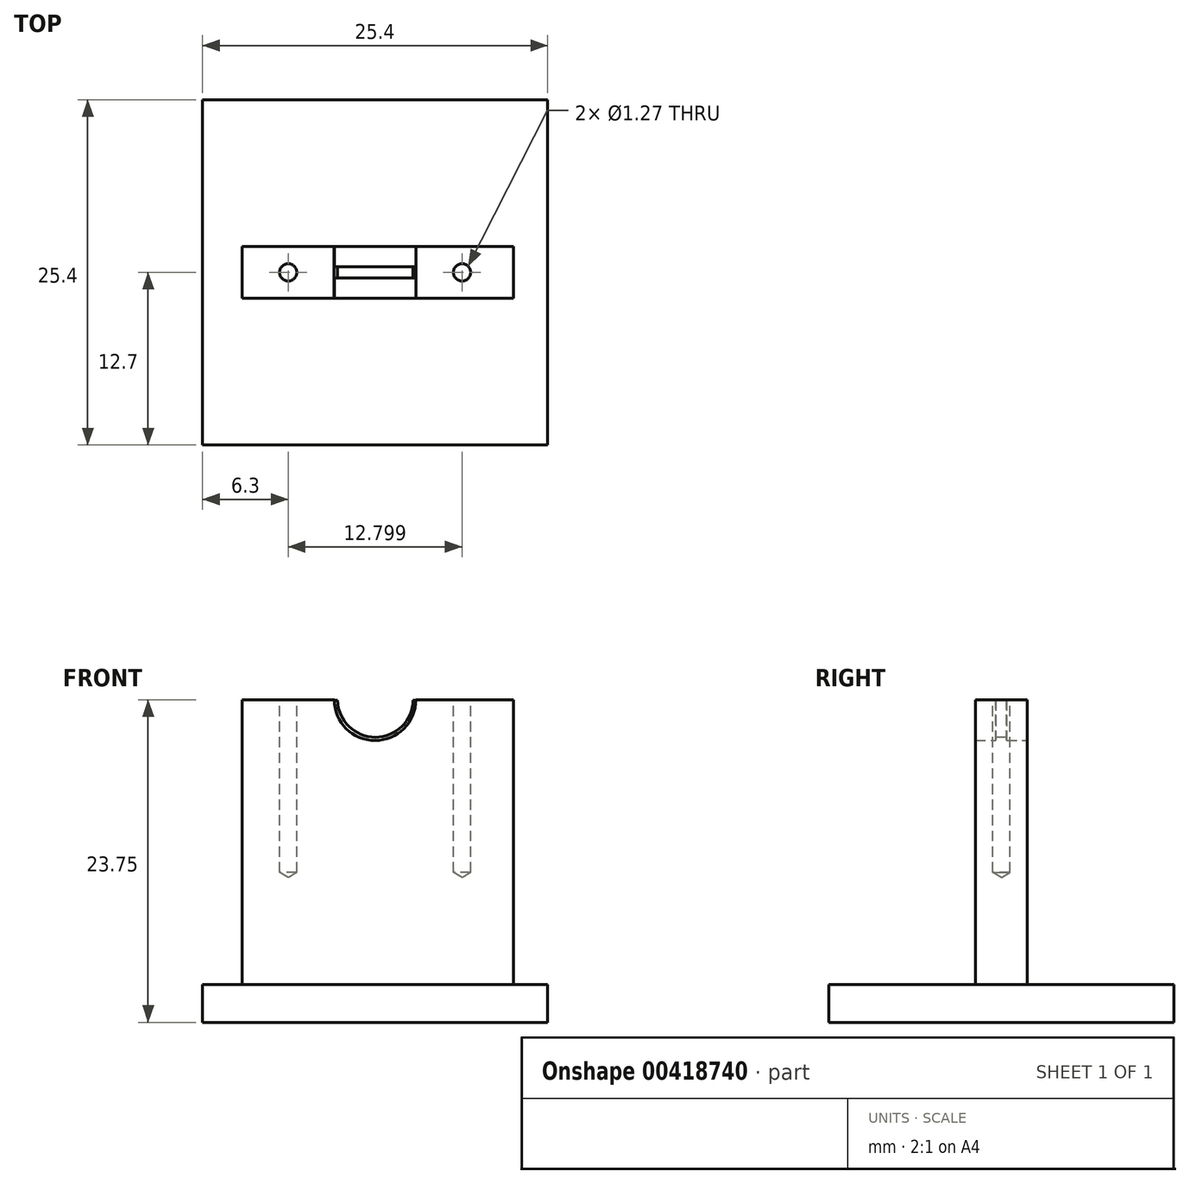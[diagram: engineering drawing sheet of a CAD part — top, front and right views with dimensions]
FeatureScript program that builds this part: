
annotation { "Feature Type Name" : "Feature", "Feature Type Description" : "" }
export const myFeature = defineFeature(function(context is Context, id is Id, definition is map)
    precondition{}
    {
        {
            var Q0;
            Q0=qCreatedBy(makeId("Top.planeOp"),FACE);
            var sketch = newSketch(context, id + "F0", { "sketchPlane" : qUnion([Q0])});
            skLineSegment(sketch, "E0.bottom", {"start": v(-12.7, 12.7) * mm, "end": v(12.7, 12.7) * mm});
            skLineSegment(sketch, "E0.top", {"start": v(-12.7, -12.7) * mm, "end": v(12.7, -12.7) * mm});
            skLineSegment(sketch, "E0.left", {"start": v(-12.7, 12.7) * mm, "end": v(-12.7, -12.7) * mm});
            skLineSegment(sketch, "E0.right", {"start": v(12.7, 12.7) * mm, "end": v(12.7, -12.7) * mm});
            skSolve(sketch);
        }
        {
            var Q0;
            Q0=makeQuery(id+"F0.imprint","IMPRINT",FACE,{"disambiguationData":[TD([[makeQuery(id+"F0.imprint","IMPRINT",EDGE,{"derivedFrom":sQuery(id+"F0.wireOp",EDGE,"E0.bottom")}),-1.0]])]});
            extrude(context, id + "F1", {"entities" : qUnion([Q0]), "depth" : 2.8 * mm});
        }
        {
            var Q0;
            Q0=qCreatedBy(makeId("Front.planeOp"),FACE);
            var sketch = newSketch(context, id + "F2", { "sketchPlane" : qUnion([Q0])});
            skLineSegment(sketch, "E1.bottom", {"start": v(-9.78, 0) * mm, "end": v(10.2, 0) * mm});
            skLineSegment(sketch, "E1.top", {"start": v(-9.78, 23.75) * mm, "end": v(10.2, 23.75) * mm});
            skLineSegment(sketch, "E1.left", {"start": v(-9.78, 0) * mm, "end": v(-9.78, 23.75) * mm});
            skLineSegment(sketch, "E1.right", {"start": v(10.2, 0) * mm, "end": v(10.2, 23.75) * mm});
            skSolve(sketch);
        }
        {
            var Q0;
            Q0=makeQuery(id+"F2.imprint","IMPRINT",FACE,{"disambiguationData":[TD([[makeQuery(id+"F2.imprint","IMPRINT",EDGE,{"derivedFrom":sQuery(id+"F2.wireOp",EDGE,"E1.bottom")}),1.0]])]});
            extrude(context, id + "F3", {"entities" : qUnion([Q0]), "operationType" : NewBodyOperationType.ADD, "depth" : 3.8 * mm, "symmetric" : true});
        }
        {
            var Q0;
            Q0=qCreatedBy(makeId("Front.planeOp"),FACE);
            var sketch = newSketch(context, id + "F4", { "sketchPlane" : qUnion([Q0])});
            skCircle(sketch, "E2", {"center": v(0, 23.75) * mm, "radius": 3 * mm});
            skSolve(sketch);
        }
        {
            var Q0;
            Q0=makeQuery(id+"F4.imprint","IMPRINT",FACE,{"disambiguationData":[TD([[makeQuery(id+"F4.imprint","IMPRINT",EDGE,{"derivedFrom":sQuery(id+"F4.wireOp",EDGE,"E2")}),1.0]])]});
            extrude(context, id + "F5", {"entities" : qUnion([Q0]), "operationType" : NewBodyOperationType.REMOVE, "depth" : 5.23 * mm, "symmetric" : true});
        }
        {
            var Q0;
            Q0=qCreatedBy(makeId("Front.planeOp"),FACE);
            var sketch = newSketch(context, id + "F6", { "sketchPlane" : qUnion([Q0])});
            skCircle(sketch, "E3", {"center": v(0, 23.76) * mm, "radius": 3.02 * mm});
            skSolve(sketch);
        }
        {
            var Q0;
            Q0=makeQuery(id+"F6.imprint","IMPRINT",FACE,{"disambiguationData":[TD([[makeQuery(id+"F6.imprint","IMPRINT",EDGE,{"derivedFrom":sQuery(id+"F6.wireOp",EDGE,"E3")}),1.0]])]});
            extrude(context, id + "F7", {"entities" : qUnion([Q0]), "operationType" : NewBodyOperationType.ADD, "depth" : .8 * mm, "symmetric" : true});
        }
        {
            var Q0;
            Q0=qCreatedBy(makeId("Front.planeOp"),FACE);
            var sketch = newSketch(context, id + "F8", { "sketchPlane" : qUnion([Q0])});
            skArc(sketch, "E4", {"start": v(-2.76, 23.7) * mm, "mid": v(0.02, 20.98) * mm, "end": v(2.8, 23.7) * mm});
            skArc(sketch, "E5.0", {"start": v(3.02, 23.75) * mm, "mid": v(0, 26.78) * mm, "end": v(-3.02, 23.75) * mm});
            skLineSegment(sketch, "E6", {"start": v(3.02, 23.75) * mm, "end": v(2.8, 23.7) * mm});
            skLineSegment(sketch, "E7", {"start": v(-2.76, 23.7) * mm, "end": v(-3.02, 23.75) * mm});
            skSolve(sketch);
        }
        {
            var Q0;
            Q0=makeQuery(id+"F8.imprint","IMPRINT",FACE,{"disambiguationData":[TD([[makeQuery(id+"F8.imprint","IMPRINT",EDGE,{"derivedFrom":sQuery(id+"F8.wireOp",EDGE,"E4")}),1.0]])]});
            extrude(context, id + "F9", {"entities" : qUnion([Q0]), "operationType" : NewBodyOperationType.REMOVE, "oppositeDirection" : true, "depth" : 25.4 * mm, "symmetric" : true});
        }
        {
            var Q0;
            {var subQ1=sQuery(id+"F2.wireOp",EDGE,"E1.left");var subQ2=sQuery(id+"F2.wireOp",EDGE,"E1.top");Q0=makeQuery(id+"F5.boolean.opBoolean","SPLIT",FACE,{"disambiguationData":[TD([makeQuery(id+"F3.opExtrude","SWEPT_FACE",FACE,{"disambiguationData":[OSD([subQ1])]})])],"derivedFrom":makeQuery(id+"F3.opExtrude","SWEPT_FACE",FACE,{"disambiguationData":[OSD([subQ2])]})});}
            var sketch = newSketch(context, id + "F10", { "sketchPlane" : qUnion([Q0])});
            skCircle(sketch, "E8", {"center": v(-6.4, 0) * mm, "radius": 0.57 * mm});
            skCircle(sketch, "E9", {"center": v(6.4, 0) * mm, "radius": 0.57 * mm});
            skSolve(sketch);
        }
        {
            var Q0;
            Q0=sQuery(id+"F10.wireOp",VERTEX,"E9.center");
            var Q1;
            Q1=sQuery(id+"F10.wireOp",VERTEX,"E8.center");
            var Q2;
            Q2=makeQuery(id+"F1.opExtrude","SWEPT_BODY",BODY,{"disambiguationData":[OSD([sQuery(id+"F0.wireOp",EDGE,"E0.bottom"),sQuery(id+"F0.wireOp",EDGE,"E0.top"),sQuery(id+"F0.wireOp",EDGE,"E0.left"),sQuery(id+"F0.wireOp",EDGE,"E0.right")])]});
            hole(context, id + "F11", {"style" : HoleStyle.SIMPLE, "endStyle" : HoleEndStyle.BLIND, "holeDiameter" : 1.27 * mm, "holeDepth" : 12.7 * mm, "isTappedThrough" : true, "tappedDepth" : 12.7 * mm, "tapClearance" : 3, "locations" : qUnion([Q0, Q1]), "scope" : qUnion([Q2])});
        }
    });
